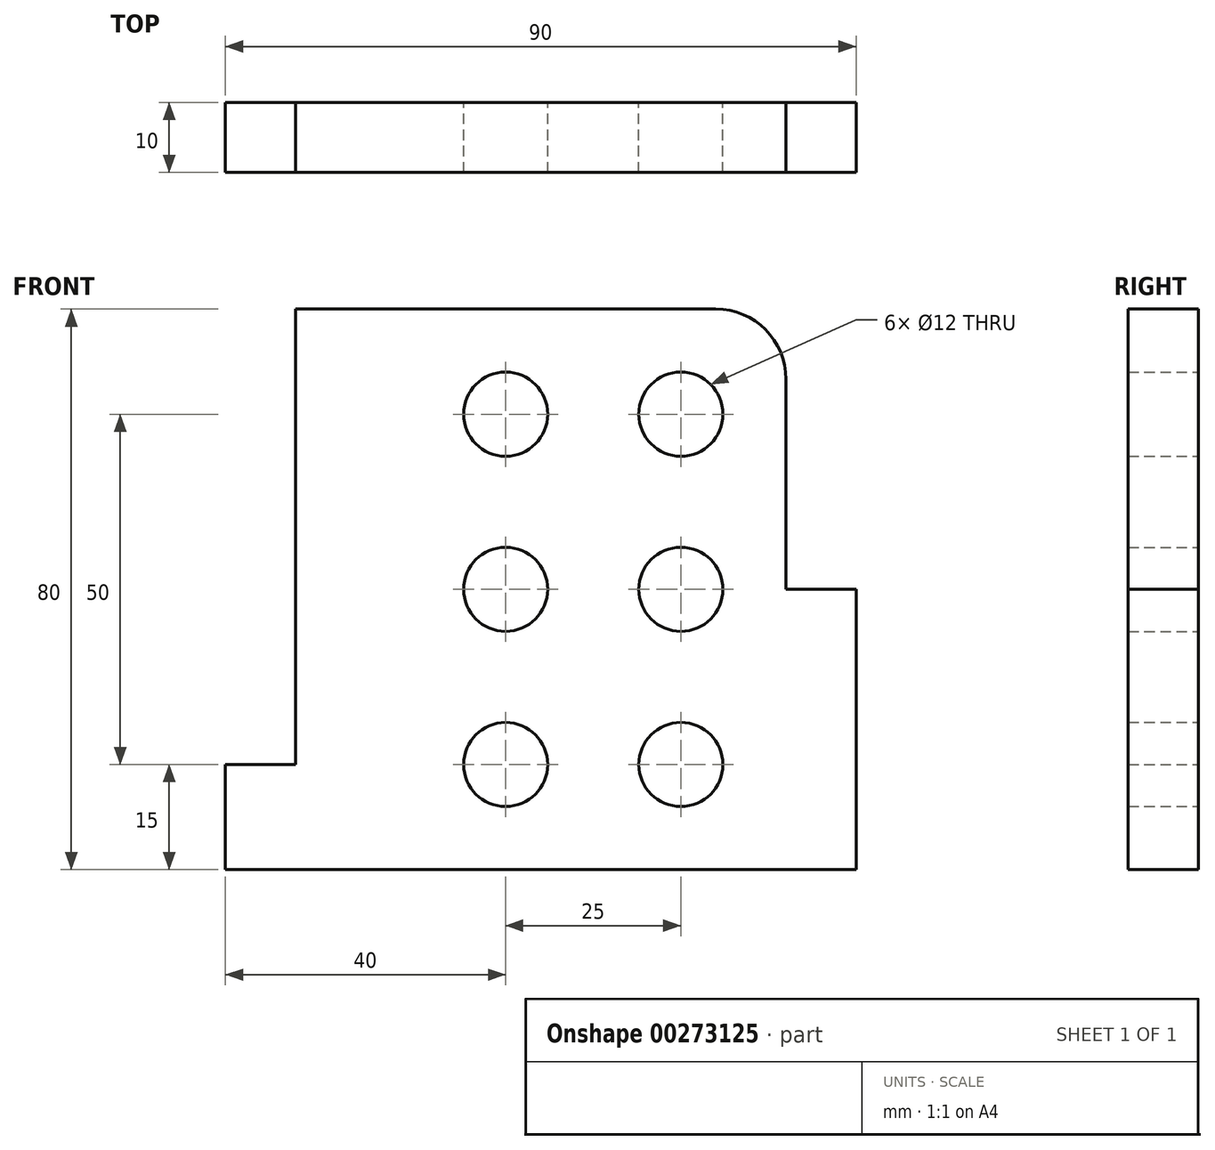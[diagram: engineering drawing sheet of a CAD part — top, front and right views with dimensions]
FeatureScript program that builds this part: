
annotation { "Feature Type Name" : "Feature", "Feature Type Description" : "" }
export const myFeature = defineFeature(function(context is Context, id is Id, definition is map)
    precondition{}
    {
        {
            var Q0;
            Q0=qCreatedBy(makeId("Front.planeOp"),FACE);
            var sketch = newSketch(context, id + "F0", { "sketchPlane" : qUnion([Q0])});
            skLineSegment(sketch, "E0", {"start": v(0, 0) * mm, "end": v(0, 15) * mm});
            skLineSegment(sketch, "E1", {"start": v(0, 15) * mm, "end": v(10, 15) * mm});
            skLineSegment(sketch, "E2", {"start": v(10, 15) * mm, "end": v(10, 80) * mm});
            skLineSegment(sketch, "E3", {"start": v(80, 40) * mm, "end": v(90, 40) * mm});
            skLineSegment(sketch, "E4", {"start": v(90, 40) * mm, "end": v(90, 0) * mm});
            skLineSegment(sketch, "E5", {"start": v(90, 0) * mm, "end": v(0, 0) * mm});
            skLineSegment(sketch, "E6", {"start": v(10, 80) * mm, "end": v(70, 80) * mm});
            skLineSegment(sketch, "E7", {"start": v(80, 40) * mm, "end": v(80, 70) * mm});
            skArc(sketch, "E8", {"start": v(80, 70) * mm, "mid": v(77.07, 77.07) * mm, "end": v(70, 80) * mm});
            skCircle(sketch, "E9", {"center": v(40, 65) * mm, "radius": 6 * mm});
            skCircle(sketch, "E10", {"center": v(65, 65) * mm, "radius": 6 * mm});
            skCircle(sketch, "E11", {"center": v(65, 40) * mm, "radius": 6 * mm});
            skCircle(sketch, "E12", {"center": v(40, 40) * mm, "radius": 6 * mm});
            skCircle(sketch, "E13", {"center": v(40, 15) * mm, "radius": 6 * mm});
            skCircle(sketch, "E14", {"center": v(65, 15) * mm, "radius": 6 * mm});
            skSolve(sketch);
        }
        {
            var Q0;
            Q0=makeQuery(id+"F0.imprint","IMPRINT",FACE,{"disambiguationData":[TD([[makeQuery(id+"F0.imprint","IMPRINT",EDGE,{"derivedFrom":sQuery(id+"F0.wireOp",EDGE,"E0")}),-1.0]])]});
            extrude(context, id + "F1", {"entities" : qUnion([Q0]), "depth" : 10 * mm});
        }
    });
